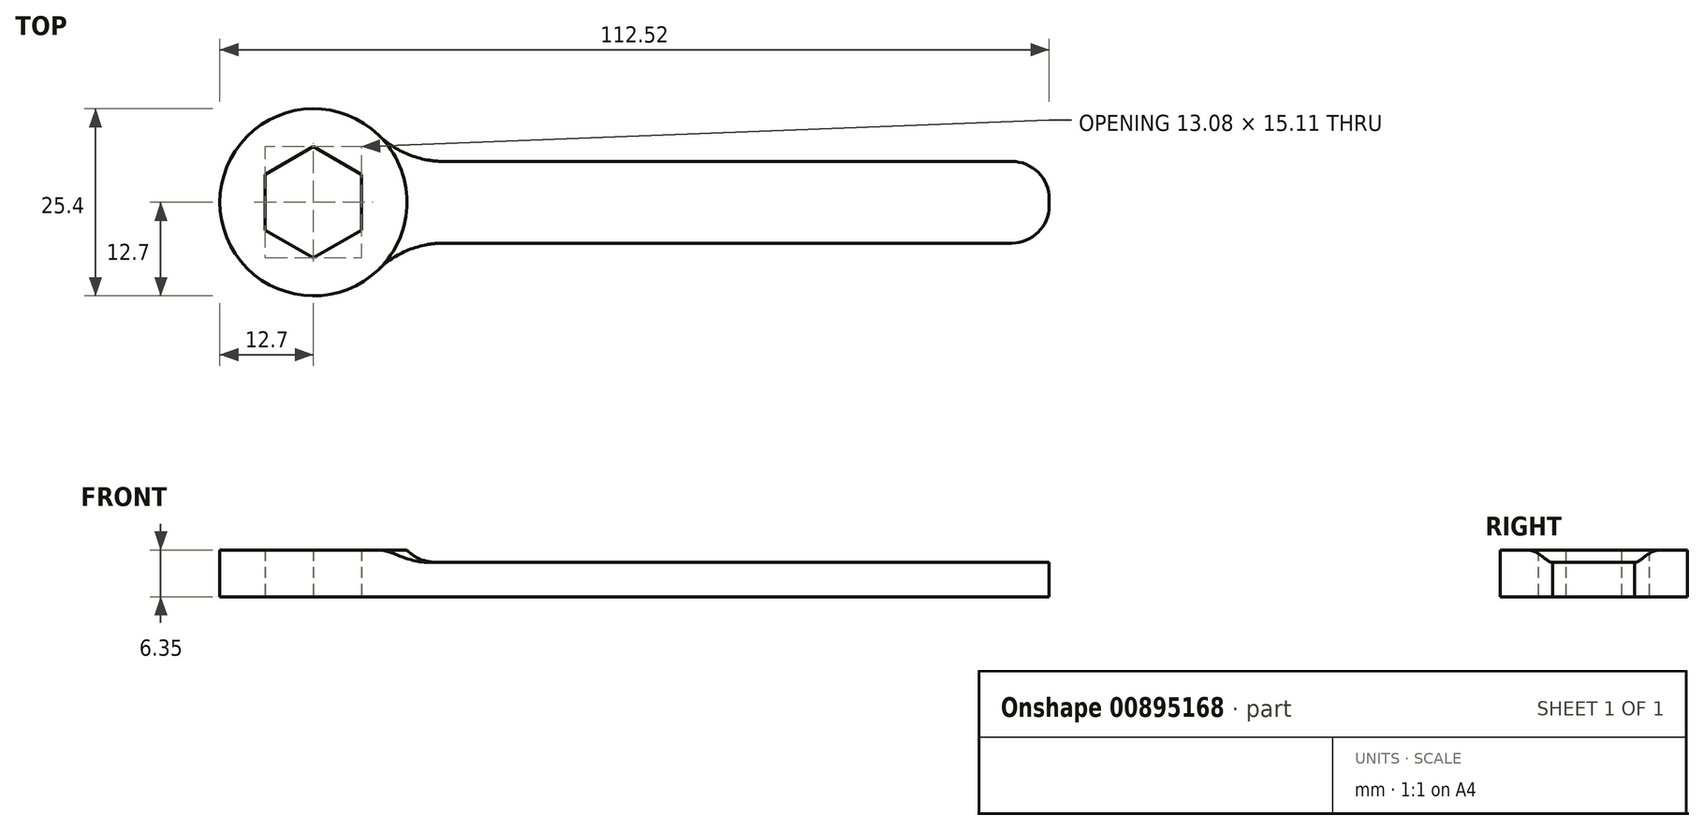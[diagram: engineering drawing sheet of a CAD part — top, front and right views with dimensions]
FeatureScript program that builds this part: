
annotation { "Feature Type Name" : "Feature", "Feature Type Description" : "" }
export const myFeature = defineFeature(function(context is Context, id is Id, definition is map)
    precondition{}
    {
        {
            var Q0;
            Q0=qCreatedBy(makeId("Top.planeOp"),FACE);
            var sketch = newSketch(context, id + "F0", { "sketchPlane" : qUnion([Q0])});
            skCircle(sketch, "E0", {"center": v(0, 0) * mm, "radius": 12.7 * mm});
            skCircle(sketch, "E1.cCircle", {"center": v(0, 0) * mm, "radius": 6.54 * mm, "construction": true});
            skLineSegment(sketch, "E1.0", {"start": v(-6.54, -3.78) * mm, "end": v(-6.54, 3.78) * mm});
            skLineSegment(sketch, "E1.1", {"start": v(-6.54, 3.78) * mm, "end": v(0, 7.55) * mm});
            skLineSegment(sketch, "E1.2", {"start": v(0, 7.55) * mm, "end": v(6.54, 3.78) * mm});
            skLineSegment(sketch, "E1.3", {"start": v(6.54, 3.78) * mm, "end": v(6.54, -3.78) * mm});
            skLineSegment(sketch, "E1.4", {"start": v(6.54, -3.78) * mm, "end": v(0, -7.55) * mm});
            skLineSegment(sketch, "E1.5", {"start": v(0, -7.55) * mm, "end": v(-6.54, -3.78) * mm});
            skPoint(sketch, "E1.0.midPoint", {"position": v(-6.54, 0) * mm});
            skSolve(sketch);
        }
        {
            var Q0;
            Q0=makeQuery(id+"F0.imprint","IMPRINT",FACE,{"disambiguationData":[TD([[makeQuery(id+"F0.imprint","IMPRINT",EDGE,{"derivedFrom":sQuery(id+"F0.wireOp",EDGE,"E0")}),1.0]])]});
            extrude(context, id + "F1", {"entities" : qUnion([Q0]), "depth" : 6.35 * mm, "offsetDistance" : 25.4 * mm});
        }
        {
            var Q0;
            Q0=qCreatedBy(makeId("Right.planeOp"),FACE);
            var sketch = newSketch(context, id + "F2", { "sketchPlane" : qUnion([Q0])});
            skLineSegment(sketch, "E2.bottom", {"start": v(-5.55, 4.68) * mm, "end": v(5.55, 4.68) * mm});
            skLineSegment(sketch, "E2.top", {"start": v(-5.55, 0) * mm, "end": v(5.55, 0) * mm});
            skLineSegment(sketch, "E2.right", {"start": v(5.55, 4.68) * mm, "end": v(5.55, 0) * mm});
            skLineSegment(sketch, "E3.MirrorCS", {"start": v(-5.55, 4.68) * mm, "end": v(-5.55, 0) * mm});
            skSolve(sketch);
        }
        {
            var Q0;
            Q0=makeQuery(id+"F2.imprint","IMPRINT",FACE,{"disambiguationData":[TD([[makeQuery(id+"F2.imprint","IMPRINT",EDGE,{"derivedFrom":sQuery(id+"F2.wireOp",EDGE,"E2.bottom")}),-1.0]])]});
            extrude(context, id + "F3", {"entities" : qUnion([Q0]), "operationType" : NewBodyOperationType.ADD, "depth" : 99.82 * mm, "offsetDistance" : 25.4 * mm, "hasSecondDirection" : true, "secondDirectionOppositeDirection" : false, "secondDirectionDepth" : 9.9 * mm});
        }
        {
            var Q0;
            Q0=makeQuery(id+"F3.boolean.opBoolean","INTERSECT",EDGE,{"derivedFrom":[makeQuery(id+"F1.opExtrude","SWEPT_FACE",FACE,{"disambiguationData":[OSD([sQuery(id+"F0.wireOp",EDGE,"E0")])]}),makeQuery(id+"F3.opExtrude","SWEPT_FACE",FACE,{"disambiguationData":[OSD([sQuery(id+"F2.wireOp",EDGE,"E2.bottom")])]})]});
            fillet(context, id + "F4", {"entities" : qUnion([Q0]), "radius" : 5.08 * mm, "tangentPropagation" : true, "allowEdgeOverflow" : false});
        }
        {
            var Q0;
            Q0=makeQuery(id+"F3.boolean.opBoolean","INTERSECT",EDGE,{"derivedFrom":[makeQuery(id+"F1.opExtrude","SWEPT_FACE",FACE,{"disambiguationData":[OSD([sQuery(id+"F0.wireOp",EDGE,"E0")])]}),makeQuery(id+"F3.opExtrude","SWEPT_FACE",FACE,{"disambiguationData":[OSD([sQuery(id+"F2.wireOp",EDGE,"E3.MirrorCS")])]})]});
            var Q1;
            Q1=makeQuery(id+"F3.boolean.opBoolean","INTERSECT",EDGE,{"derivedFrom":[makeQuery(id+"F1.opExtrude","SWEPT_FACE",FACE,{"disambiguationData":[OSD([sQuery(id+"F0.wireOp",EDGE,"E0")])]}),makeQuery(id+"F3.opExtrude","SWEPT_FACE",FACE,{"disambiguationData":[OSD([sQuery(id+"F2.wireOp",EDGE,"E2.right")])]})]});
            fillet(context, id + "F5", {"entities" : qUnion([Q0, Q1]), "radius" : 12.7 * mm, "tangentPropagation" : true, "allowEdgeOverflow" : false});
        }
        {
            var Q0;
            Q0=makeQuery(id+"F3.opExtrude","CAP_EDGE",EDGE,{"disambiguationData":[OSD([sQuery(id+"F2.wireOp",EDGE,"E3.MirrorCS")])],"isStart":false});
            var Q1;
            Q1=makeQuery(id+"F3.opExtrude","CAP_EDGE",EDGE,{"disambiguationData":[OSD([sQuery(id+"F2.wireOp",EDGE,"E2.right")])],"isStart":false});
            fillet(context, id + "F6", {"entities" : qUnion([Q0, Q1]), "radius" : 5.08 * mm, "tangentPropagation" : true, "allowEdgeOverflow" : false});
        }
    });
